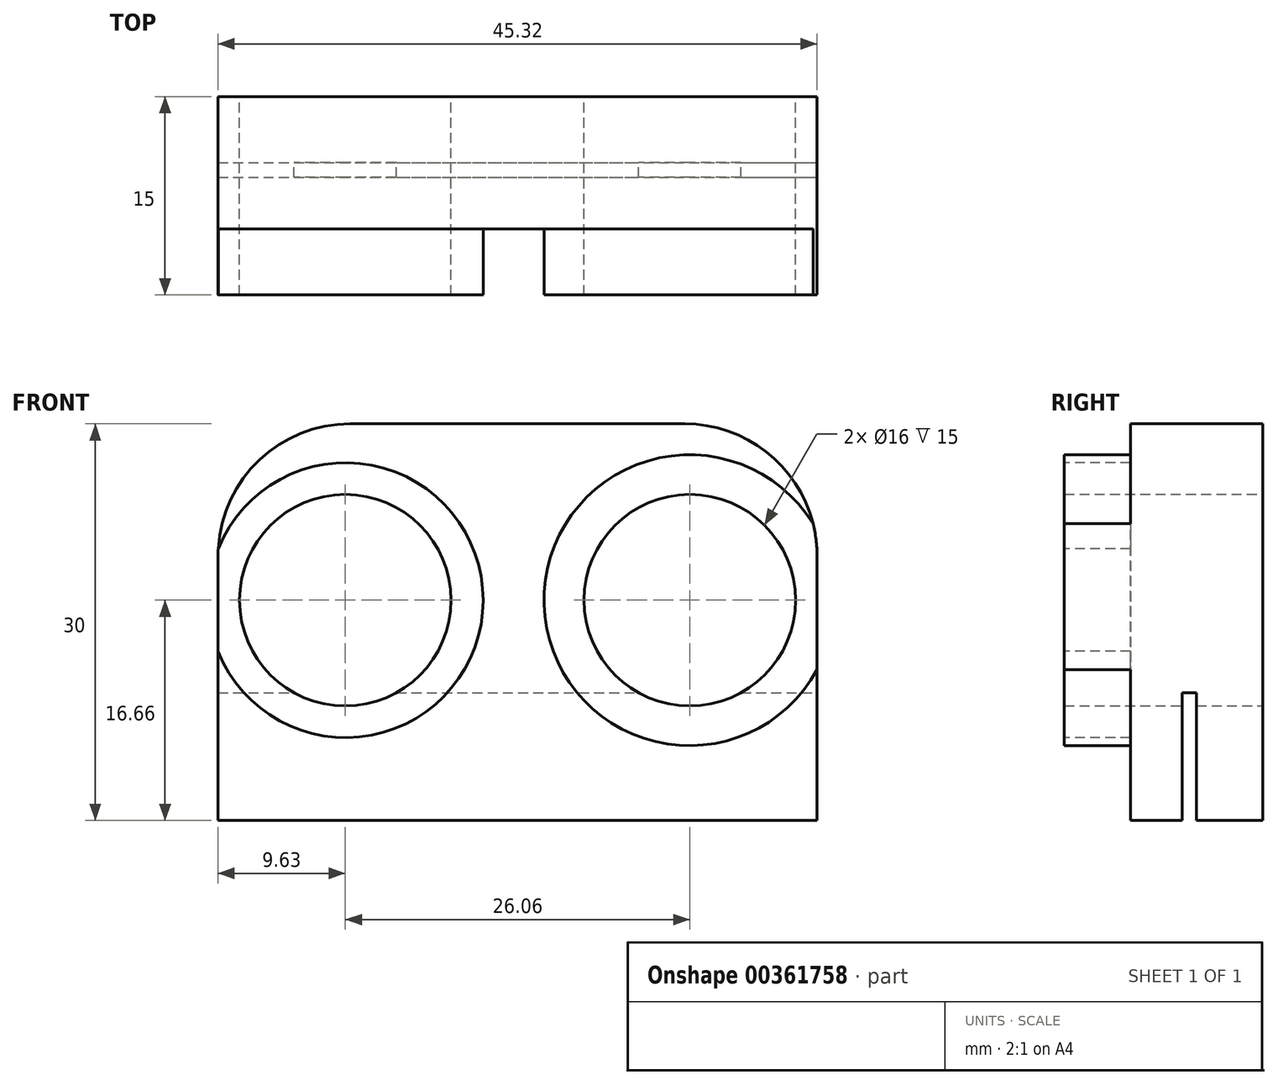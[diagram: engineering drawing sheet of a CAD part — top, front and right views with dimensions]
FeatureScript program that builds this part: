
annotation { "Feature Type Name" : "Feature", "Feature Type Description" : "" }
export const myFeature = defineFeature(function(context is Context, id is Id, definition is map)
    precondition{}
    {
        {
            var Q0;
            Q0=qCreatedBy(makeId("Front.planeOp"),FACE);
            var sketch = newSketch(context, id + "F0", { "sketchPlane" : qUnion([Q0])});
            skCircle(sketch, "E0", {"center": v(-13.03, 0) * mm, "radius": 8 * mm});
            skCircle(sketch, "E1", {"center": v(13.03, 0) * mm, "radius": 8 * mm});
            skLineSegment(sketch, "E2.bottom", {"start": v(22.66, -16.66) * mm, "end": v(-22.65, -16.66) * mm});
            skLineSegment(sketch, "E2.top", {"start": v(22.66, 13.34) * mm, "end": v(-22.66, 13.34) * mm});
            skLineSegment(sketch, "E2.left", {"start": v(22.66, -16.66) * mm, "end": v(22.66, 13.34) * mm});
            skLineSegment(sketch, "E2.right", {"start": v(-22.65, -16.66) * mm, "end": v(-22.66, 13.34) * mm});
            skSolve(sketch);
        }
        {
            var Q0;
            Q0=makeQuery(id+"F0.imprint","IMPRINT",FACE,{"disambiguationData":[TD([[makeQuery(id+"F0.imprint","IMPRINT",EDGE,{"derivedFrom":sQuery(id+"F0.wireOp",EDGE,"E0")}),-1.0]])]});
            extrude(context, id + "F1", {"entities" : qUnion([Q0]), "depth" : 15 * mm, "offsetDistance" : 25 * mm});
        }
        {
            var Q0;
            Q0=qCreatedBy(makeId("Right.planeOp"),FACE);
            var sketch = newSketch(context, id + "F2", { "sketchPlane" : qUnion([Q0])});
            skLineSegment(sketch, "E3", {"start": v(-5, -19) * mm, "end": v(-5, -7) * mm});
            skLineSegment(sketch, "E4", {"start": v(-5, -7) * mm, "end": v(-6.1, -7) * mm});
            skLineSegment(sketch, "E5", {"start": v(-5, -19) * mm, "end": v(-6.1, -19) * mm});
            skLineSegment(sketch, "E6", {"start": v(-6.1, -19) * mm, "end": v(-6.1, -7) * mm});
            skSolve(sketch);
        }
        {
            var Q0;
            Q0=makeQuery(id+"F2.imprint","IMPRINT",FACE,{"disambiguationData":[TD([[makeQuery(id+"F2.imprint","IMPRINT",EDGE,{"derivedFrom":sQuery(id+"F2.wireOp",EDGE,"E3")}),1.0]])]});
            extrude(context, id + "F3", {"entities" : qUnion([Q0]), "operationType" : NewBodyOperationType.REMOVE, "oppositeDirection" : true, "depth" : 25 * mm, "offsetDistance" : 25 * mm, "hasSecondDirection" : true, "secondDirectionOppositeDirection" : false, "secondDirectionDepth" : 25 * mm});
        }
        {
            var Q0;
            Q0=qCreatedBy(makeId("Front.planeOp"),FACE);
            cPlane(context, id + "F4", {"entities" : qUnion([Q0]), "cplaneType" : CPlaneType.OFFSET, "offset" : 15 * mm, "width" : 150 * mm, "height" : 150 * mm});
        }
        {
            var Q0;
            Q0=qCreatedBy(id+"F4.planeOp",FACE);
            var sketch = newSketch(context, id + "F5", { "sketchPlane" : qUnion([Q0])});
            skCircle(sketch, "E7", {"center": v(-13, 0) * mm, "radius": 10.4 * mm});
            skCircle(sketch, "E8", {"center": v(13, 0) * mm, "radius": 11 * mm});
            skLineSegment(sketch, "E9.bottom", {"start": v(32.15, -21.48) * mm, "end": v(-26.9, -21.48) * mm});
            skLineSegment(sketch, "E9.top", {"start": v(32.15, 22.96) * mm, "end": v(-26.9, 22.96) * mm});
            skLineSegment(sketch, "E9.left", {"start": v(32.15, -21.48) * mm, "end": v(32.15, 22.96) * mm});
            skLineSegment(sketch, "E9.right", {"start": v(-26.9, -21.48) * mm, "end": v(-26.9, 22.96) * mm});
            skSolve(sketch);
        }
        {
            var Q0;
            Q0=makeQuery(id+"F5.imprint","IMPRINT",FACE,{"disambiguationData":[TD([[makeQuery(id+"F5.imprint","IMPRINT",EDGE,{"derivedFrom":sQuery(id+"F5.wireOp",EDGE,"E7")}),-1.0]])]});
            extrude(context, id + "F6", {"entities" : qUnion([Q0]), "operationType" : NewBodyOperationType.REMOVE, "oppositeDirection" : true, "depth" : 5 * mm, "offsetDistance" : 25 * mm});
        }
        {
            var Q0;
            Q0=makeQuery(id+"F1.opExtrude","SWEPT_EDGE",EDGE,{"disambiguationData":[OSD([sQuery(id+"F0.wireOp",EDGE,"E2.top"),sQuery(id+"F0.wireOp",EDGE,"E2.left")])]});
            var Q1;
            Q1=makeQuery(id+"F1.opExtrude","SWEPT_EDGE",EDGE,{"disambiguationData":[OSD([sQuery(id+"F0.wireOp",EDGE,"E2.top"),sQuery(id+"F0.wireOp",EDGE,"E2.right")])]});
            fillet(context, id + "F7", {"entities" : qUnion([Q0, Q1]), "radius" : 10 * mm, "tangentPropagation" : true, "allowEdgeOverflow" : false});
        }
    });
